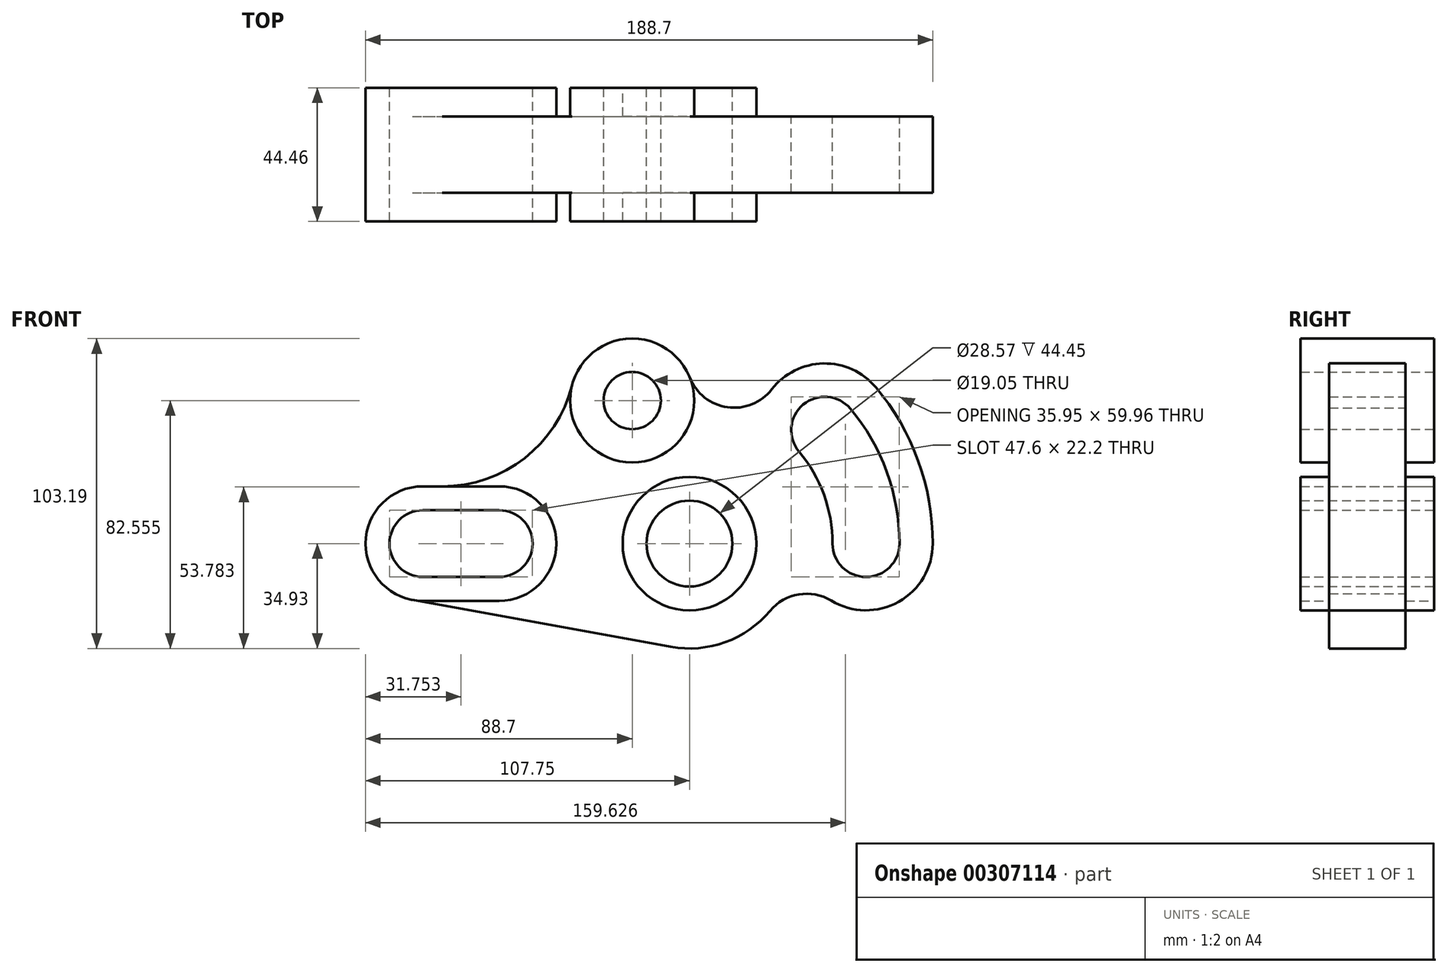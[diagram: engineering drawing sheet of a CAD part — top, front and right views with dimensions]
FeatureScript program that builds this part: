
annotation { "Feature Type Name" : "Feature", "Feature Type Description" : "" }
export const myFeature = defineFeature(function(context is Context, id is Id, definition is map)
    precondition{}
    {
        {
            var Q0;
            Q0=qCreatedBy(makeId("Front.planeOp"),FACE);
            var sketch = newSketch(context, id + "F0", { "sketchPlane" : qUnion([Q0])});
            skCircle(sketch, "E0", {"center": v(0, 0) * mm, "radius": 22.23 * mm});
            skLineSegment(sketch, "E1", {"start": v(0, 0) * mm, "end": v(117.45, 0) * mm, "construction": true});
            skLineSegment(sketch, "E2", {"start": v(0, 0) * mm, "end": v(-144.07, 0) * mm, "construction": true});
            skLineSegment(sketch, "E3", {"start": v(0, 105.83) * mm, "end": v(0, -100.4) * mm, "construction": true});
            skCircle(sketch, "E4", {"center": v(-19.05, 47.63) * mm, "radius": 9.53 * mm});
            skCircle(sketch, "E5", {"center": v(-19.05, 47.63) * mm, "radius": 20.64 * mm});
            skLineSegment(sketch, "E6", {"start": v(0, 0) * mm, "end": v(107.02, 89.8) * mm, "construction": true});
            skArc(sketch, "E7", {"start": v(47.6, 0) * mm, "mid": v(58.72, -11.13) * mm, "end": v(69.85, 0) * mm});
            skArc(sketch, "E8.trimOffspring", {"start": v(58.72, 0) * mm, "mid": v(55.18, 20.09) * mm, "end": v(44.99, 37.75) * mm, "construction": true});
            skArc(sketch, "E9", {"start": v(53.5, 44.9) * mm, "mid": v(37.83, 46.27) * mm, "end": v(36.46, 30.6) * mm});
            skArc(sketch, "E10", {"start": v(47.6, 0) * mm, "mid": v(44.73, 16.28) * mm, "end": v(36.46, 30.6) * mm});
            skArc(sketch, "E11", {"start": v(69.85, 0) * mm, "mid": v(65.64, 23.9) * mm, "end": v(53.5, 44.9) * mm});
            skPoint(sketch, "E12", {"position": v(-88.7, 0) * mm});
            skPoint(sketch, "E13", {"position": v(-63.3, 0) * mm});
            skArc(sketch, "E14", {"start": v(-88.7, 11.1) * mm, "mid": v(-99.8, 0) * mm, "end": v(-88.7, -11.1) * mm});
            skArc(sketch, "E15", {"start": v(-63.3, -11.1) * mm, "mid": v(-52.2, 0) * mm, "end": v(-63.3, 11.1) * mm});
            skLineSegment(sketch, "E16", {"start": v(-88.7, 11.1) * mm, "end": v(-63.3, 11.1) * mm});
            skLineSegment(sketch, "E17", {"start": v(-88.7, -11.1) * mm, "end": v(-63.3, -11.1) * mm});
            skArc(sketch, "E18", {"start": v(-88.7, 19.05) * mm, "mid": v(-107.75, 0) * mm, "end": v(-88.7, -19.05) * mm});
            skArc(sketch, "E19", {"start": v(-63.3, -19.05) * mm, "mid": v(-44.25, 0) * mm, "end": v(-63.3, 19.05) * mm});
            skLineSegment(sketch, "E20", {"start": v(-88.7, 19.05) * mm, "end": v(-63.3, 19.05) * mm});
            skLineSegment(sketch, "E21", {"start": v(-88.7, -19.05) * mm, "end": v(-63.3, -19.05) * mm});
            skArc(sketch, "E22", {"start": v(-82.17, 19.05) * mm, "mid": v(-54.84, 28.45) * mm, "end": v(-39.06, 52.66) * mm});
            skArc(sketch, "E23.0", {"start": v(62.01, 52.03) * mm, "mid": v(44.56, 59.97) * mm, "end": v(27.43, 51.37) * mm});
            skArc(sketch, "E23.1", {"start": v(80.95, 0) * mm, "mid": v(76.07, 27.69) * mm, "end": v(62.01, 52.03) * mm});
            skArc(sketch, "E23.2", {"start": v(47.2, -19) * mm, "mid": v(69.63, -19.36) * mm, "end": v(80.95, 0) * mm});
            skArc(sketch, "E24", {"start": v(0.13, 55.24) * mm, "mid": v(12.65, 45.39) * mm, "end": v(27.43, 51.37) * mm});
            skLineSegment(sketch, "E25", {"start": v(-92.1, -18.74) * mm, "end": v(-6.25, -34.36) * mm});
            skArc(sketch, "E26", {"start": v(-6.25, -34.36) * mm, "mid": v(11.89, -32.84) * mm, "end": v(26.8, -22.4) * mm});
            skArc(sketch, "E27", {"start": v(47.2, -19) * mm, "mid": v(36.37, -16.92) * mm, "end": v(26.8, -22.4) * mm});
            skCircle(sketch, "E28", {"center": v(0, 0) * mm, "radius": 14.29 * mm});
            skSolve(sketch);
        }
        {
            var Q0;
            Q0=makeQuery(id+"F0.imprint","IMPRINT",FACE,{"disambiguationData":[TD([[makeQuery(id+"F0.imprint","IMPRINT",EDGE,{"derivedFrom":sQuery(id+"F0.wireOp",EDGE,"E0")}),-1.0]])]});
            extrude(context, id + "F1", {"entities" : qUnion([Q0]), "depth" : 25.4 * mm, "symmetric" : true});
        }
        {
            var Q0;
            Q0=makeQuery(id+"F0.imprint","IMPRINT",FACE,{"disambiguationData":[TD([[makeQuery(id+"F0.imprint","IMPRINT",EDGE,{"derivedFrom":sQuery(id+"F0.wireOp",EDGE,"E14")}),-1.0]])]});
            var Q1;
            Q1=makeQuery(id+"F0.imprint","IMPRINT",FACE,{"disambiguationData":[TD([[makeQuery(id+"F0.imprint","IMPRINT",EDGE,{"derivedFrom":sQuery(id+"F0.wireOp",EDGE,"E0")}),1.0]])]});
            var Q2;
            Q2=makeQuery(id+"F0.imprint","IMPRINT",FACE,{"disambiguationData":[TD([[makeQuery(id+"F0.imprint","IMPRINT",EDGE,{"derivedFrom":sQuery(id+"F0.wireOp",EDGE,"E4")}),-1.0]])]});
            extrude(context, id + "F2", {"entities" : qUnion([Q0, Q1, Q2]), "operationType" : NewBodyOperationType.ADD, "depth" : 44.45 * mm, "symmetric" : true});
        }
    });
